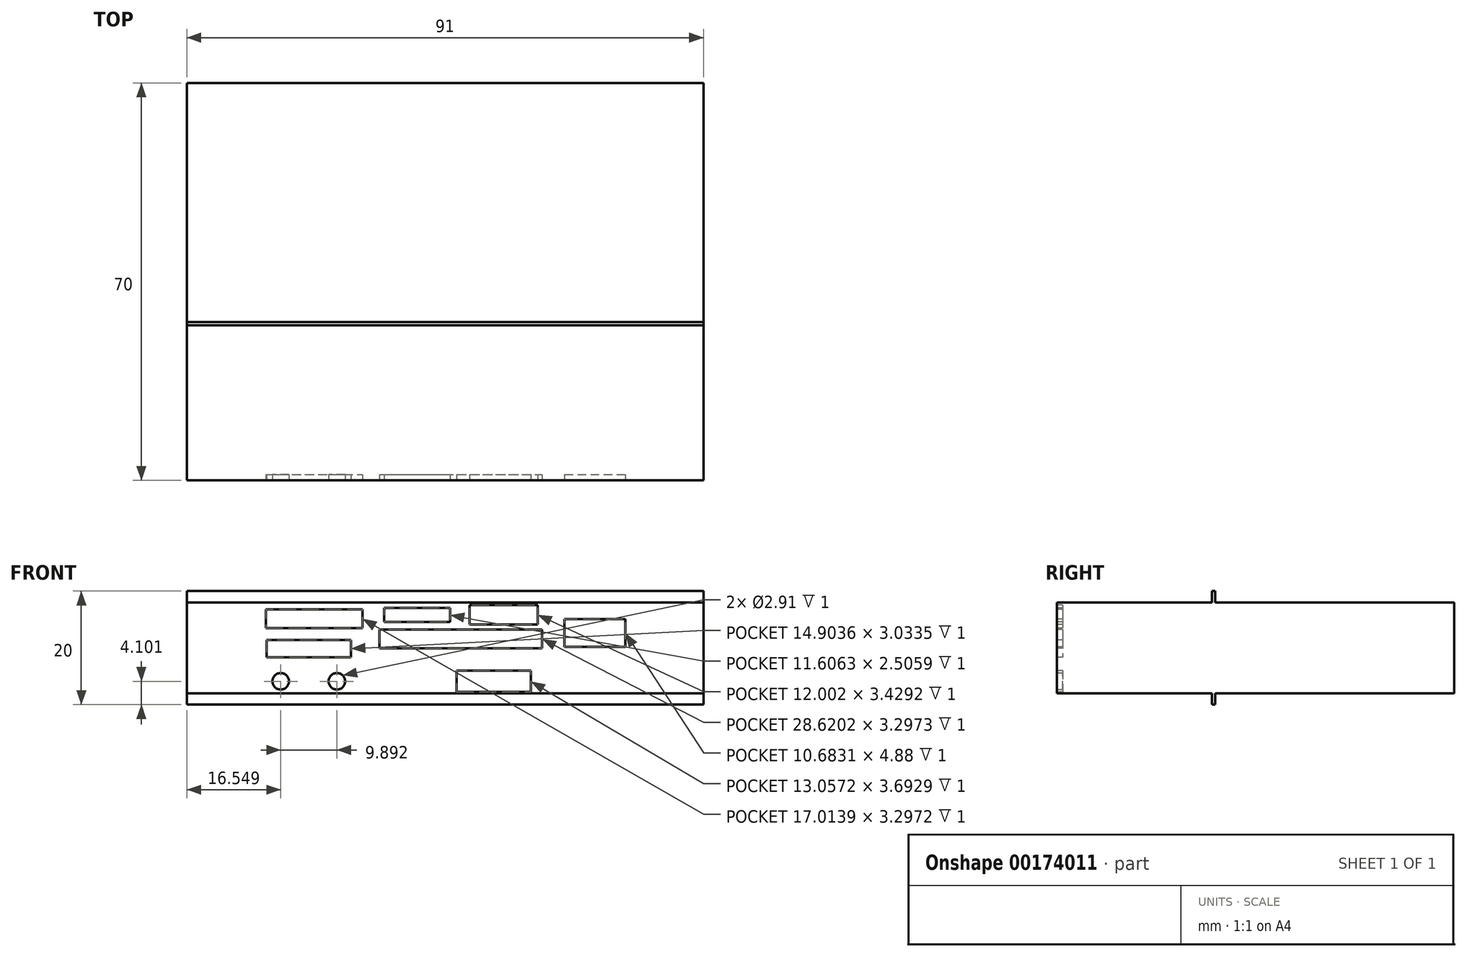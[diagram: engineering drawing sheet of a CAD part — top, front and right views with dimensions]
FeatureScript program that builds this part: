
annotation { "Feature Type Name" : "Feature", "Feature Type Description" : "" }
export const myFeature = defineFeature(function(context is Context, id is Id, definition is map)
    precondition{}
    {
        {
            var Q0;
            Q0=qCreatedBy(makeId("Front.planeOp"),FACE);
            var sketch = newSketch(context, id + "F0", { "sketchPlane" : qUnion([Q0])});
            skLineSegment(sketch, "E0.bottom", {"start": v(45.5, 8) * mm, "end": v(-45.5, 8) * mm});
            skLineSegment(sketch, "E0.top", {"start": v(45.5, -8) * mm, "end": v(-45.5, -8) * mm});
            skLineSegment(sketch, "E0.left", {"start": v(45.5, 8) * mm, "end": v(45.5, -8) * mm});
            skLineSegment(sketch, "E0.right", {"start": v(-45.5, 8) * mm, "end": v(-45.5, -8) * mm});
            skPoint(sketch, "E0.middle", {"position": v(0, 0) * mm});
            skSolve(sketch);
        }
        {
            var Q0;
            Q0 = qSketchRegion(id + "F0", true);
            extrude(context, id + "F1", {"entities" : qUnion([Q0]), "oppositeDirection" : true, "depth" : 70 * mm});
        }
        {
            var Q0;
            Q0=makeQuery(id+"F1.opExtrude","CAP_FACE",FACE,{"disambiguationData":[OSD([sQuery(id+"F0.wireOp",EDGE,"E0.bottom"),sQuery(id+"F0.wireOp",EDGE,"E0.top"),sQuery(id+"F0.wireOp",EDGE,"E0.left"),sQuery(id+"F0.wireOp",EDGE,"E0.right")])],"isStart":true});
            var sketch = newSketch(context, id + "F2", { "sketchPlane" : qUnion([Q0])});
            skCircle(sketch, "E1", {"center": v(-28.95, -5.9) * mm, "radius": 1.46 * mm});
            skCircle(sketch, "E2", {"center": v(-19.06, -5.9) * mm, "radius": 1.46 * mm});
            skLineSegment(sketch, "E3.bottom", {"start": v(21.04, 5.05) * mm, "end": v(31.72, 5.05) * mm});
            skLineSegment(sketch, "E3.top", {"start": v(21.04, 0.17) * mm, "end": v(31.72, 0.17) * mm});
            skLineSegment(sketch, "E3.left", {"start": v(21.04, 5.05) * mm, "end": v(21.04, 0.17) * mm});
            skLineSegment(sketch, "E3.right", {"start": v(31.72, 5.05) * mm, "end": v(31.72, 0.17) * mm});
            skLineSegment(sketch, "E4.bottom", {"start": v(2.04, -4.05) * mm, "end": v(15.1, -4.05) * mm});
            skLineSegment(sketch, "E4.top", {"start": v(2.04, -7.75) * mm, "end": v(15.1, -7.75) * mm});
            skLineSegment(sketch, "E4.left", {"start": v(2.04, -4.05) * mm, "end": v(2.04, -7.75) * mm});
            skLineSegment(sketch, "E4.right", {"start": v(15.1, -4.05) * mm, "end": v(15.1, -7.75) * mm});
            skLineSegment(sketch, "E5.bottom", {"start": v(-31.59, 6.76) * mm, "end": v(-14.58, 6.76) * mm});
            skLineSegment(sketch, "E5.top", {"start": v(-31.59, 3.47) * mm, "end": v(-14.58, 3.47) * mm});
            skLineSegment(sketch, "E5.left", {"start": v(-31.59, 6.76) * mm, "end": v(-31.59, 3.47) * mm});
            skLineSegment(sketch, "E5.right", {"start": v(-14.58, 6.76) * mm, "end": v(-14.58, 3.47) * mm});
            skLineSegment(sketch, "E6.bottom", {"start": v(-31.46, 1.36) * mm, "end": v(-16.55, 1.36) * mm});
            skLineSegment(sketch, "E6.top", {"start": v(-31.46, -1.68) * mm, "end": v(-16.55, -1.68) * mm});
            skLineSegment(sketch, "E6.left", {"start": v(-31.46, 1.36) * mm, "end": v(-31.46, -1.68) * mm});
            skLineSegment(sketch, "E6.right", {"start": v(-16.55, 1.36) * mm, "end": v(-16.55, -1.68) * mm});
            skLineSegment(sketch, "E7.bottom", {"start": v(-10.75, 7.03) * mm, "end": v(0.86, 7.03) * mm});
            skLineSegment(sketch, "E7.top", {"start": v(-10.75, 4.52) * mm, "end": v(0.86, 4.52) * mm});
            skLineSegment(sketch, "E7.left", {"start": v(-10.75, 7.03) * mm, "end": v(-10.75, 4.52) * mm});
            skLineSegment(sketch, "E7.right", {"start": v(0.86, 7.03) * mm, "end": v(0.86, 4.52) * mm});
            skLineSegment(sketch, "E8.bottom", {"start": v(4.29, 7.55) * mm, "end": v(16.29, 7.55) * mm});
            skLineSegment(sketch, "E8.top", {"start": v(4.29, 4.13) * mm, "end": v(16.29, 4.13) * mm});
            skLineSegment(sketch, "E8.left", {"start": v(4.29, 7.55) * mm, "end": v(4.29, 4.13) * mm});
            skLineSegment(sketch, "E8.right", {"start": v(16.29, 7.55) * mm, "end": v(16.29, 4.13) * mm});
            skLineSegment(sketch, "E9.bottom", {"start": v(-11.54, 3.2) * mm, "end": v(17.08, 3.2) * mm});
            skLineSegment(sketch, "E9.top", {"start": v(-11.54, -0.1) * mm, "end": v(17.08, -0.1) * mm});
            skLineSegment(sketch, "E9.left", {"start": v(-11.54, 3.2) * mm, "end": v(-11.54, -0.1) * mm});
            skLineSegment(sketch, "E9.right", {"start": v(17.08, 3.2) * mm, "end": v(17.08, -0.1) * mm});
            skSolve(sketch);
        }
        {
            var Q0;
            Q0 = qSketchRegion(id + "F2", true);
            extrude(context, id + "F3", {"entities" : qUnion([Q0]), "operationType" : NewBodyOperationType.REMOVE, "oppositeDirection" : true, "depth" : 1 * mm});
        }
        {
            var Q0;
            Q0=makeQuery(id+"F1.opExtrude","SWEPT_FACE",FACE,{"disambiguationData":[OSD([sQuery(id+"F0.wireOp",EDGE,"E0.left")])]});
            var sketch = newSketch(context, id + "F4", { "sketchPlane" : qUnion([Q0])});
            skLineSegment(sketch, "E10.bottom", {"start": v(27.3, 8) * mm, "end": v(27.9, 8) * mm});
            skLineSegment(sketch, "E10.top", {"start": v(27.3, 10) * mm, "end": v(27.9, 10) * mm});
            skLineSegment(sketch, "E10.left", {"start": v(27.3, 8) * mm, "end": v(27.3, 10) * mm});
            skLineSegment(sketch, "E10.right", {"start": v(27.9, 8) * mm, "end": v(27.9, 10) * mm});
            skLineSegment(sketch, "E11.bottom", {"start": v(27.3, -8) * mm, "end": v(27.9, -8) * mm});
            skLineSegment(sketch, "E11.top", {"start": v(27.3, -10) * mm, "end": v(27.9, -10) * mm});
            skLineSegment(sketch, "E11.left", {"start": v(27.3, -8) * mm, "end": v(27.3, -10) * mm});
            skLineSegment(sketch, "E11.right", {"start": v(27.9, -8) * mm, "end": v(27.9, -10) * mm});
            skSolve(sketch);
        }
        {
            var Q0;
            Q0 = qSketchRegion(id + "F4", true);
            var Q1;
            Q1=makeQuery(id+"F1.opExtrude","SWEPT_FACE",FACE,{"disambiguationData":[OSD([sQuery(id+"F0.wireOp",EDGE,"E0.right")])]});
            extrude(context, id + "F5", {"entities" : qUnion([Q0]), "operationType" : NewBodyOperationType.ADD, "endBound" : BoundingType.UP_TO_SURFACE, "oppositeDirection" : true, "endBoundEntityFace" : qUnion([Q1]), "depth" : 25 * mm});
        }
    });
